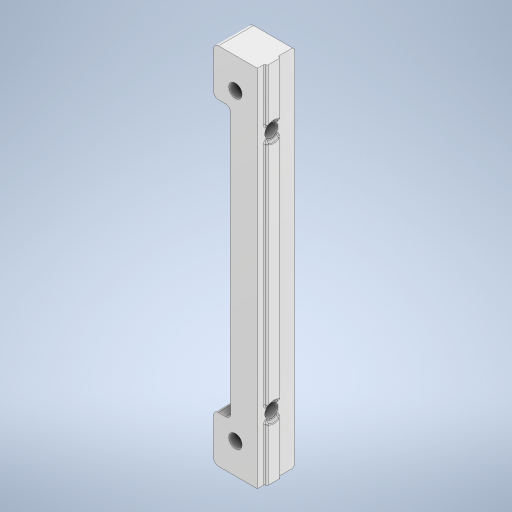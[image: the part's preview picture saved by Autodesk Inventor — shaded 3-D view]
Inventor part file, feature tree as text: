
AUTODESK INVENTOR PART (.ipt)
format: ipt  version: 2024 (Build 280153000, 153)  size: 523,776 bytes
history: native  units: mm
features: sketch x6, extrude x5, projected_geometry x4, fillet x3, hole x2, chamfer x2
ambient origin geometry x8: Origin, YZ Plane, XZ Plane, XY Plane, X Axis, Y Axis, Z Axis, Center Point
bodies: Solid1 (feature_tree)
feature tree (22):
  sketch  "Sketch1"  dims[d2=18.0mm d3=150.0mm]
  extrude  "Extrusion1"  Depth=150.0mm
  hole  "Hole1"  [1 undecoded]
  extrude  "Extrusion3"  Depth=2.0mm
  hole  "Hole2"  [1 undecoded]
  extrude  "Extrusion4"  Depth=2.0mm
  fillet  "Fillet3"  Radius=5.75mm
  extrude  "Extrusion5"  Depth=2.0mm TaperAngle=0.0deg
  extrude  "Extrusion6"  Depth=2.0mm
  chamfer  "Chamfer1"  Distance=10.0mm
  fillet  "Fillet4"  [1 undecoded]
  fillet  "Fillet5"  Radius=6.0mm
  chamfer  "Chamfer2"  Distance=6.0mm
  sketch  "Sketch5"  dims[d4=125.0mm d5=5.75mm d6=0.0mm]
  projected_geometry  "Projected Loop1"
  sketch  "Sketch6"  dims[d7=9.75mm d8=0.0mm]
  sketch  "Sketch7"  dims[d9=5.4mm d10=6.0mm d11=4.0mm d12=2.0mm d13=90.0deg d14=8.0mm d15=150.0deg d22=8.25mm]
  projected_geometry  "Projected Loop2"
  sketch  "Sketch8"  dims[d23=8.0mm d24=0.0mm d25=100.0mm]
  projected_geometry  "Projected Loop3"
  sketch  "Sketch9"  dims[d26=5.4mm d27=6.0mm d28=4.0mm d29=2.0mm d30=90.0deg d31=8.0mm d32=150.0deg d35=5.75mm d36=5.75mm d37=7.0mm d38=0.0mm d39=2.0mm d40=10.0mm d41=0.0mm d42=0.0mm d43=6.0mm d44=6.0mm d45=5.5mm d46=1.0mm d47=0.0mm d48=1.0mm d49=2.0mm d50=45.0deg d51=0.5mm d52=0.5mm d53=1.0mm d54=2.0mm d55=45.0deg]
  projected_geometry  "Projected Loop4"
note: 3 required parameter values undecoded (feature->parameter linkage not recoverable at this tier; creation-order binding heuristic only, values carry confidence <= 0.55)
